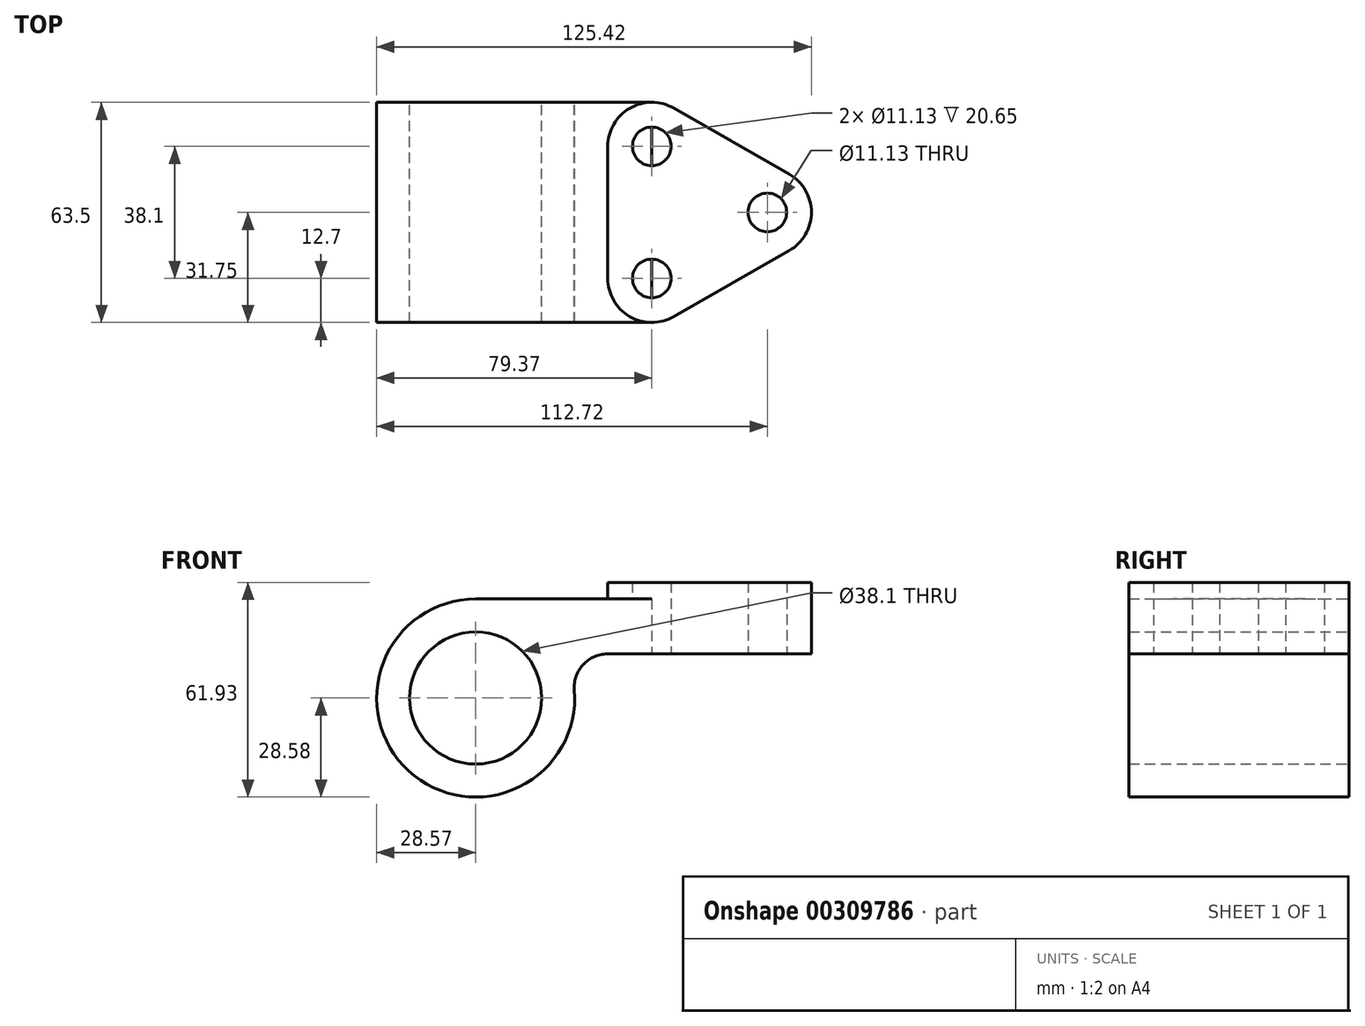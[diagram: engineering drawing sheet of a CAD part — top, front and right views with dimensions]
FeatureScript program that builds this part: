
annotation { "Feature Type Name" : "Feature", "Feature Type Description" : "" }
export const myFeature = defineFeature(function(context is Context, id is Id, definition is map)
    precondition{}
    {
        {
            var Q0;
            Q0=qCreatedBy(makeId("Front.planeOp"),FACE);
            var sketch = newSketch(context, id + "F0", { "sketchPlane" : qUnion([Q0])});
            skCircle(sketch, "E0", {"center": v(0, 0) * mm, "radius": 19.05 * mm});
            skArc(sketch, "E1", {"start": v(0, 28.58) * mm, "mid": v(-19.35, -21.03) * mm, "end": v(28.48, 2.38) * mm});
            skLineSegment(sketch, "E2", {"start": v(37.97, 12.7) * mm, "end": v(50.8, 12.7) * mm});
            skLineSegment(sketch, "E3", {"start": v(50.8, 12.7) * mm, "end": v(50.8, 28.58) * mm});
            skLineSegment(sketch, "E4", {"start": v(50.8, 28.58) * mm, "end": v(0, 28.58) * mm});
            skArc(sketch, "E5", {"start": v(37.97, 12.7) * mm, "mid": v(30.96, 9.62) * mm, "end": v(28.48, 2.38) * mm});
            skSolve(sketch);
        }
        {
            var Q0;
            Q0=makeQuery(id+"F0.imprint","IMPRINT",FACE,{"disambiguationData":[TD([[makeQuery(id+"F0.imprint","IMPRINT",EDGE,{"derivedFrom":sQuery(id+"F0.wireOp",EDGE,"E0")}),-1.0]])]});
            extrude(context, id + "F1", {"entities" : qUnion([Q0]), "depth" : 63.5 * mm});
        }
        {
            var Q0;
            Q0=makeQuery(id+"F1.opExtrude","SWEPT_FACE",FACE,{"disambiguationData":[OSD([sQuery(id+"F0.wireOp",EDGE,"E2")])]});
            var sketch = newSketch(context, id + "F2", { "sketchPlane" : qUnion([Q0])});
            skCircle(sketch, "E6", {"center": v(50.8, 50.8) * mm, "radius": 5.56 * mm});
            skCircle(sketch, "E7", {"center": v(50.8, 12.7) * mm, "radius": 5.56 * mm});
            skArc(sketch, "E8", {"start": v(57.1, 61.83) * mm, "mid": v(44.42, 61.78) * mm, "end": v(38.1, 50.8) * mm});
            skArc(sketch, "E9", {"start": v(38.1, 12.7) * mm, "mid": v(44.42, 1.72) * mm, "end": v(57.1, 1.67) * mm});
            skLineSegment(sketch, "E10", {"start": v(50.8, 50.8) * mm, "end": v(35, 50.8) * mm, "construction": true});
            skLineSegment(sketch, "E11", {"start": v(50.8, 12.7) * mm, "end": v(33.22, 12.7) * mm, "construction": true});
            skLineSegment(sketch, "E12", {"start": v(38.1, 12.7) * mm, "end": v(38.1, 50.8) * mm});
            skCircle(sketch, "E13", {"center": v(84.15, 31.75) * mm, "radius": 5.56 * mm});
            skArc(sketch, "E14", {"start": v(90.45, 20.72) * mm, "mid": v(96.85, 31.75) * mm, "end": v(90.45, 42.78) * mm});
            skLineSegment(sketch, "E15", {"start": v(90.45, 42.78) * mm, "end": v(57.1, 61.83) * mm});
            skLineSegment(sketch, "E16", {"start": v(57.1, 1.67) * mm, "end": v(90.45, 20.72) * mm});
            skSolve(sketch);
        }
        {
            var Q0;
            {var subQ4=sQuery(id+"F2.wireOp",EDGE,"E12");Q0=makeQuery(id+"F2.imprint","IMPRINT",FACE,{"disambiguationData":[TD([[makeQuery(id+"F2.imprint","IMPRINT",EDGE,{"derivedFrom":subQ4}),-1.0]])]});}
            var Q1;
            Q1=makeQuery(id+"F2.imprint","IMPRINT",FACE,{"disambiguationData":[TD([[makeQuery(id+"F2.imprint","IMPRINT",EDGE,{"derivedFrom":sQuery(id+"F2.wireOp",EDGE,"E13")}),-1.0]])]});
            extrude(context, id + "F3", {"entities" : qUnion([Q0, Q1]), "operationType" : NewBodyOperationType.ADD, "oppositeDirection" : true, "depth" : 20.65 * mm});
        }
    });
